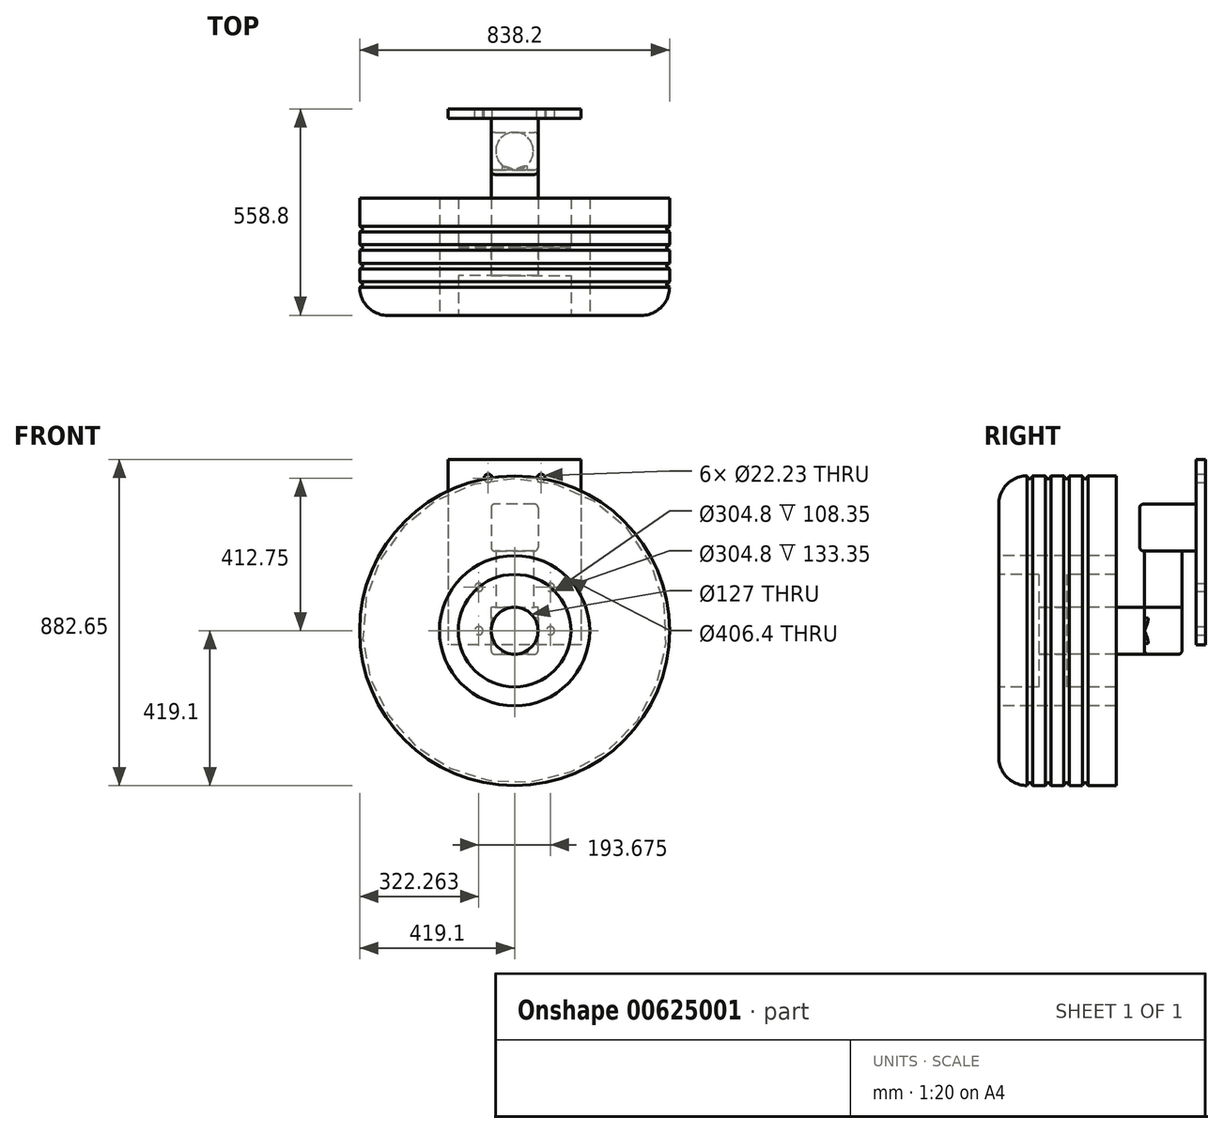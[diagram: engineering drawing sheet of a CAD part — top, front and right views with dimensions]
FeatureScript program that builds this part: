
annotation { "Feature Type Name" : "Feature", "Feature Type Description" : "" }
export const myFeature = defineFeature(function(context is Context, id is Id, definition is map)
    precondition{}
    {
        {
            var Q0;
            Q0=qCreatedBy(makeId("Right.planeOp"),FACE);
            var sketch = newSketch(context, id + "F0", { "sketchPlane" : qUnion([Q0])});
            skLineSegment(sketch, "E0", {"start": v(-439.18, 0) * mm, "end": v(305.36, 0) * mm, "construction": true});
            skLineSegment(sketch, "E1", {"start": v(-158.75, 203.2) * mm, "end": v(-158.75, 152.4) * mm});
            skLineSegment(sketch, "E2", {"start": v(-158.75, 203.2) * mm, "end": v(158.75, 203.2) * mm});
            skLineSegment(sketch, "E3", {"start": v(158.75, 203.2) * mm, "end": v(158.75, 152.4) * mm});
            skLineSegment(sketch, "E4", {"start": v(0, 509.7) * mm, "end": v(0, -178.07) * mm, "construction": true});
            skPoint(sketch, "E5", {"position": v(0, 203.2) * mm});
            skLineSegment(sketch, "E6", {"start": v(-25.4, 0) * mm, "end": v(25.4, 0) * mm});
            skLineSegment(sketch, "E7", {"start": v(158.75, 152.4) * mm, "end": v(25.4, 152.4) * mm});
            skLineSegment(sketch, "E8", {"start": v(25.4, 152.4) * mm, "end": v(25.4, 0) * mm});
            skLineSegment(sketch, "E9.MirrorCS", {"start": v(-25.4, 152.4) * mm, "end": v(-25.4, 0) * mm});
            skLineSegment(sketch, "E10.MirrorCS", {"start": v(-158.75, 152.4) * mm, "end": v(-25.4, 152.4) * mm});
            skSolve(sketch);
        }
        {
            var Q0;
            Q0 = qSketchRegion(id + "F0", true);
            var Q1;
            Q1=sQuery(id+"F0.wireOp",EDGE,"E0");
            revolve(context, id + "F1", {"surfaceOperationType" : NewSurfaceOperationType.NEW, "entities" : qUnion([Q0]), "axis" : qUnion([Q1]), "revolveType" : RevolveType.FULL});
        }
        {
            var Q0;
            Q0=makeQuery(id+"F1.opRevolve","SWEPT_FACE",FACE,{"disambiguationData":[OSD([sQuery(id+"F0.wireOp",EDGE,"E8")])]});
            var sketch = newSketch(context, id + "F2", { "sketchPlane" : qUnion([Q0])});
            skCircle(sketch, "E11", {"center": v(0, 0) * mm, "radius": 63.5 * mm});
            skSolve(sketch);
        }
        {
            var Q0;
            Q0 = qSketchRegion(id + "F2", true);
            extrude(context, id + "F3", {"entities" : qUnion([Q0]), "operationType" : NewBodyOperationType.REMOVE, "endBound" : BoundingType.THROUGH_ALL, "oppositeDirection" : true, "depth" : 25 * mm, "offsetDistance" : 25 * mm});
        }
        {
            var Q0;
            Q0=makeQuery(id+"F1.opRevolve","SWEPT_FACE",FACE,{"disambiguationData":[OSD([sQuery(id+"F0.wireOp",EDGE,"E9.MirrorCS")])]});
            extrude(context, id + "F4", {"entities" : qUnion([Q0]), "operationType" : NewBodyOperationType.ADD, "depth" : 25 * mm, "offsetDistance" : 25 * mm});
        }
        {
            var Q0;
            Q0=makeQuery(id+"F4.opExtrude","CAP_FACE",FACE,{"disambiguationData":[OSD([sQuery(id+"F0.wireOp",EDGE,"E9.MirrorCS")])],"isStart":false});
            var sketch = newSketch(context, id + "F5", { "sketchPlane" : qUnion([Q0])});
            skCircle(sketch, "E12", {"center": v(0, 0) * mm, "radius": 63.5 * mm});
            skSolve(sketch);
        }
        {
            var Q0;
            Q0 = qSketchRegion(id + "F5", true);
            extrude(context, id + "F6", {"entities" : qUnion([Q0]), "oppositeDirection" : true, "depth" : 285.75 * mm, "offsetDistance" : 25 * mm});
        }
        {
            var Q0;
            Q0=makeQuery(id+"F1.opRevolve","SWEPT_FACE",FACE,{"disambiguationData":[OSD([sQuery(id+"F0.wireOp",EDGE,"E1")])]});
            var sketch = newSketch(context, id + "F7", { "sketchPlane" : qUnion([Q0])});
            skCircle(sketch, "E13", {"center": v(0, 0) * mm, "radius": 203.2 * mm});
            skCircle(sketch, "E14", {"center": v(0, 0) * mm, "radius": 419.1 * mm});
            skSolve(sketch);
        }
        {
            var Q0;
            Q0 = qSketchRegion(id + "F7", true);
            var Q1;
            Q1=makeQuery(id+"F1.opRevolve","SWEPT_FACE",FACE,{"disambiguationData":[OSD([sQuery(id+"F0.wireOp",EDGE,"E3")])]});
            extrude(context, id + "F8", {"entities" : qUnion([Q0]), "endBound" : BoundingType.UP_TO_SURFACE, "oppositeDirection" : true, "depth" : 25 * mm, "endBoundEntityFace" : qUnion([Q1]), "offsetDistance" : 25 * mm});
        }
        {
            var Q0;
            Q0=makeQuery(id+"F8.opExtrude","CAP_EDGE",EDGE,{"disambiguationData":[OSD([sQuery(id+"F7.wireOp",EDGE,"E14")])],"isStart":true});
            var Q1;
            Q1=makeQuery(id+"F8.opExtrude","TWEAK_EDGE",EDGE,{"derivedFrom":[makeQuery(id+"F1.opRevolve","SWEPT_FACE",FACE,{"disambiguationData":[OSD([sQuery(id+"F0.wireOp",EDGE,"E3")])]}),makeQuery(id+"F7.imprint","IMPRINT",EDGE,{"derivedFrom":sQuery(id+"F7.wireOp",EDGE,"E14")})]});
            fillet(context, id + "F9", {"entities" : qUnion([Q0, Q1]), "radius" : 76.2 * mm, "tangentPropagation" : true, "allowEdgeOverflow" : false});
        }
        {
            var Q0;
            Q0=qCreatedBy(makeId("Right.planeOp"),FACE);
            var sketch = newSketch(context, id + "F10", { "sketchPlane" : qUnion([Q0])});
            skPoint(sketch, "E15.middle", {"position": v(0, 0) * mm});
            skLineSegment(sketch, "E16", {"start": v(-287.93, 419.1) * mm, "end": v(273.21, 419.1) * mm, "construction": true});
            skLineSegment(sketch, "E17", {"start": v(-540.82, 0) * mm, "end": v(556.4, 0) * mm, "construction": true});
            skLineSegment(sketch, "E18", {"start": v(268.1, 406.4) * mm, "end": v(-286.95, 406.4) * mm, "construction": true});
            skLineSegment(sketch, "E19", {"start": v(-82.71, 419.1) * mm, "end": v(-82.71, 406.4) * mm, "construction": true});
            skLineSegment(sketch, "E20", {"start": v(-82.71, 419.1) * mm, "end": v(-79.47, 413.64) * mm});
            skLineSegment(sketch, "E21", {"start": v(-70.87, 413.64) * mm, "end": v(-67.63, 419.1) * mm});
            skLineSegment(sketch, "E22", {"start": v(-67.63, 419.1) * mm, "end": v(-82.71, 419.1) * mm});
            skPoint(sketch, "E23.visualSharp", {"position": v(-75.17, 406.4) * mm});
            skArc(sketch, "E23.filletArc", {"start": v(-79.47, 413.64) * mm, "mid": v(-75.17, 411.2) * mm, "end": v(-70.87, 413.64) * mm});
            skLineSegment(sketch, "E24", {"start": v(0, 0) * mm, "end": v(0, 599.85) * mm, "construction": true});
            skLineSegment(sketch, "E25", {"start": v(-82.71, 419.1) * mm, "end": v(-67.63, 419.1) * mm});
            skArc(sketch, "E26.1.0.0", {"start": v(-29.47, 413.64) * mm, "mid": v(-25.17, 411.2) * mm, "end": v(-20.87, 413.64) * mm});
            skLineSegment(sketch, "E26.1.0.1", {"start": v(-32.71, 419.1) * mm, "end": v(-29.47, 413.64) * mm});
            skLineSegment(sketch, "E26.1.0.2", {"start": v(-20.87, 413.64) * mm, "end": v(-17.63, 419.1) * mm});
            skLineSegment(sketch, "E26.1.0.3", {"start": v(-32.71, 419.1) * mm, "end": v(-17.63, 419.1) * mm});
            skArc(sketch, "E26.2.0.0", {"start": v(20.53, 413.64) * mm, "mid": v(24.83, 411.2) * mm, "end": v(29.13, 413.64) * mm});
            skLineSegment(sketch, "E26.2.0.1", {"start": v(17.29, 419.1) * mm, "end": v(20.53, 413.64) * mm});
            skLineSegment(sketch, "E26.2.0.2", {"start": v(29.13, 413.64) * mm, "end": v(32.37, 419.1) * mm});
            skLineSegment(sketch, "E26.2.0.3", {"start": v(17.29, 419.1) * mm, "end": v(32.37, 419.1) * mm});
            skArc(sketch, "E26.3.0.0", {"start": v(70.53, 413.64) * mm, "mid": v(74.83, 411.2) * mm, "end": v(79.13, 413.64) * mm});
            skLineSegment(sketch, "E26.3.0.1", {"start": v(67.29, 419.1) * mm, "end": v(70.53, 413.64) * mm});
            skLineSegment(sketch, "E26.3.0.2", {"start": v(79.13, 413.64) * mm, "end": v(82.37, 419.1) * mm});
            skLineSegment(sketch, "E26.3.0.3", {"start": v(67.29, 419.1) * mm, "end": v(82.37, 419.1) * mm});
            skLineSegment(sketch, "E26.direction1", {"start": v(-79.47, 413.64) * mm, "end": v(-29.47, 413.64) * mm, "construction": true});
            skSolve(sketch);
        }
        {
            var Q0;
            Q0 = qSketchRegion(id + "F10", true);
            var Q1;
            Q1=sQuery(id+"F10.wireOp",EDGE,"E17");
            revolve(context, id + "F11", {"operationType" : NewBodyOperationType.REMOVE, "surfaceOperationType" : NewSurfaceOperationType.NEW, "entities" : qUnion([Q0]), "axis" : qUnion([Q1]), "revolveType" : RevolveType.FULL, "oppositeDirection" : true});
        }
        {
            var Q0;
            Q0=makeQuery(id+"F6.opExtrude","CAP_FACE",FACE,{"disambiguationData":[OSD([sQuery(id+"F5.wireOp",EDGE,"E12")])],"isStart":false});
            var sketch = newSketch(context, id + "F12", { "sketchPlane" : qUnion([Q0])});
            skLineSegment(sketch, "E27.bottom", {"start": v(63.5, -63.5) * mm, "end": v(-63.5, -63.5) * mm});
            skLineSegment(sketch, "E27.top", {"start": v(63.5, 63.5) * mm, "end": v(-63.5, 63.5) * mm});
            skLineSegment(sketch, "E27.left", {"start": v(63.5, -63.5) * mm, "end": v(63.5, 63.5) * mm});
            skLineSegment(sketch, "E27.right", {"start": v(-63.5, -63.5) * mm, "end": v(-63.5, 63.5) * mm});
            skPoint(sketch, "E27.middle", {"position": v(0, 0) * mm});
            skSolve(sketch);
        }
        {
            var Q0;
            Q0 = qSketchRegion(id + "F12", true);
            extrude(context, id + "F13", {"entities" : qUnion([Q0]), "operationType" : NewBodyOperationType.ADD, "depth" : 101.6 * mm, "offsetDistance" : 25 * mm});
        }
        {
            var Q0;
            Q0=makeQuery(id+"F13.opExtrude","SWEPT_FACE",FACE,{"disambiguationData":[OSD([sQuery(id+"F12.wireOp",EDGE,"E27.top")])]});
            var sketch = newSketch(context, id + "F14", { "sketchPlane" : qUnion([Q0])});
            skCircle(sketch, "E28", {"center": v(0, 286.15) * mm, "radius": 50.8 * mm});
            skSolve(sketch);
        }
        {
            var Q0;
            Q0 = qSketchRegion(id + "F14", true);
            extrude(context, id + "F15", {"entities" : qUnion([Q0]), "operationType" : NewBodyOperationType.ADD, "depth" : 152.4 * mm, "offsetDistance" : 25 * mm});
        }
        {
            var Q0;
            Q0=makeQuery(id+"F15.opExtrude","CAP_FACE",FACE,{"disambiguationData":[OSD([sQuery(id+"F14.wireOp",EDGE,"E28")])],"isStart":false});
            var sketch = newSketch(context, id + "F16", { "sketchPlane" : qUnion([Q0])});
            skLineSegment(sketch, "E29.bottom", {"start": v(63.5, 349.65) * mm, "end": v(-63.5, 349.65) * mm});
            skLineSegment(sketch, "E29.top", {"start": v(63.5, 222.65) * mm, "end": v(-63.5, 222.65) * mm});
            skLineSegment(sketch, "E29.left", {"start": v(63.5, 349.65) * mm, "end": v(63.5, 222.65) * mm});
            skLineSegment(sketch, "E29.right", {"start": v(-63.5, 349.65) * mm, "end": v(-63.5, 222.65) * mm});
            skPoint(sketch, "E29.middle", {"position": v(0, 286.15) * mm});
            skSolve(sketch);
        }
        {
            var Q0;
            Q0 = qSketchRegion(id + "F16", true);
            extrude(context, id + "F17", {"entities" : qUnion([Q0]), "operationType" : NewBodyOperationType.ADD, "depth" : 127 * mm, "offsetDistance" : 25 * mm});
        }
        {
            var Q0;
            Q0=makeQuery(id+"F17.opExtrude","SWEPT_FACE",FACE,{"disambiguationData":[OSD([sQuery(id+"F16.wireOp",EDGE,"E29.bottom")])]});
            extrude(context, id + "F18", {"entities" : qUnion([Q0]), "operationType" : NewBodyOperationType.ADD, "depth" : 25 * mm, "offsetDistance" : 25 * mm});
        }
        {
            var Q0;
            Q0=makeQuery(id+"F18.opExtrude","CAP_FACE",FACE,{"disambiguationData":[OSD([sQuery(id+"F16.wireOp",EDGE,"E29.bottom")])],"isStart":false});
            var sketch = newSketch(context, id + "F19", { "sketchPlane" : qUnion([Q0])});
            skLineSegment(sketch, "E30.bottom", {"start": v(-179.39, 463.55) * mm, "end": v(179.39, 463.55) * mm});
            skLineSegment(sketch, "E30.top", {"start": v(-179.39, -38.1) * mm, "end": v(179.39, -38.1) * mm});
            skLineSegment(sketch, "E30.left", {"start": v(-179.39, 463.55) * mm, "end": v(-179.39, -38.1) * mm});
            skLineSegment(sketch, "E30.right", {"start": v(179.39, 463.55) * mm, "end": v(179.39, -38.1) * mm});
            skLineSegment(sketch, "E31", {"start": v(0, 463.55) * mm, "end": v(0, -82.83) * mm, "construction": true});
            skLineSegment(sketch, "E32", {"start": v(-556.4, 0) * mm, "end": v(580.96, 0) * mm, "construction": true});
            skSolve(sketch);
        }
        {
            var Q0;
            Q0 = qSketchRegion(id + "F19", true);
            extrude(context, id + "F20", {"entities" : qUnion([Q0]), "operationType" : NewBodyOperationType.ADD, "depth" : 25.4 * mm, "offsetDistance" : 25 * mm});
        }
        {
            var Q0;
            {var subQ0=sQuery(id+"F16.wireOp",EDGE,"E29.left");var subQ1=sQuery(id+"F16.wireOp",EDGE,"E29.bottom");Q0=makeQuery(id+"F18.boolean.opBoolean","MERGE",EDGE,{"derivedFrom":[makeQuery(id+"F17.opExtrude","CAP_EDGE",EDGE,{"disambiguationData":[OSD([subQ0])],"isStart":false}),makeQuery(id+"F18.opExtrude","SWEPT_EDGE",EDGE,{"disambiguationData":[OSD([subQ1,subQ0]),TDD([makeQuery(id+"F17.opExtrude","CAP_VERTEX",VERTEX,{"disambiguationData":[OSD([subQ1,subQ0])],"isStart":false})])]})]});}
            var Q1;
            {var subQ0=sQuery(id+"F16.wireOp",EDGE,"E29.right");var subQ1=sQuery(id+"F16.wireOp",EDGE,"E29.bottom");Q1=makeQuery(id+"F18.boolean.opBoolean","MERGE",EDGE,{"derivedFrom":[makeQuery(id+"F17.opExtrude","CAP_EDGE",EDGE,{"disambiguationData":[OSD([subQ0])],"isStart":false}),makeQuery(id+"F18.opExtrude","SWEPT_EDGE",EDGE,{"disambiguationData":[OSD([subQ1,subQ0]),TDD([makeQuery(id+"F17.opExtrude","CAP_VERTEX",VERTEX,{"disambiguationData":[OSD([subQ1,subQ0])],"isStart":false})])]})]});}
            var Q2;
            Q2=makeQuery(id+"F17.opExtrude","SWEPT_EDGE",EDGE,{"disambiguationData":[OSD([sQuery(id+"F16.wireOp",EDGE,"E29.top"),sQuery(id+"F16.wireOp",EDGE,"E29.left")])]});
            var Q3;
            Q3=makeQuery(id+"F17.opExtrude","SWEPT_EDGE",EDGE,{"disambiguationData":[OSD([sQuery(id+"F16.wireOp",EDGE,"E29.top"),sQuery(id+"F16.wireOp",EDGE,"E29.right")])]});
            var Q4;
            Q4=makeQuery(id+"F13.opExtrude","SWEPT_EDGE",EDGE,{"disambiguationData":[OSD([sQuery(id+"F12.wireOp",EDGE,"E27.bottom"),sQuery(id+"F12.wireOp",EDGE,"E27.right")])]});
            var Q5;
            Q5=makeQuery(id+"F13.opExtrude","SWEPT_EDGE",EDGE,{"disambiguationData":[OSD([sQuery(id+"F12.wireOp",EDGE,"E27.bottom"),sQuery(id+"F12.wireOp",EDGE,"E27.left")])]});
            var Q6;
            Q6=makeQuery(id+"F13.opExtrude","CAP_EDGE",EDGE,{"disambiguationData":[OSD([sQuery(id+"F12.wireOp",EDGE,"E27.right")])],"isStart":false});
            var Q7;
            Q7=makeQuery(id+"F13.opExtrude","CAP_EDGE",EDGE,{"disambiguationData":[OSD([sQuery(id+"F12.wireOp",EDGE,"E27.left")])],"isStart":false});
            var Q8;
            {var subQ0=sQuery(id+"F12.wireOp",EDGE,"E27.bottom");var subQ1=sQuery(id+"F12.wireOp",EDGE,"E27.right");Q8=makeQuery(id+"F13.boolean.opBoolean","SPLIT",EDGE,{"disambiguationData":[TD([makeQuery(id+"F13.opExtrude","SWEPT_FACE",FACE,{"disambiguationData":[OSD([subQ0])]})])],"derivedFrom":makeQuery(id+"F13.opExtrude","CAP_EDGE",EDGE,{"disambiguationData":[OSD([subQ1])],"isStart":true})});}
            var Q9;
            {var subQ0=sQuery(id+"F12.wireOp",EDGE,"E27.right");var subQ1=sQuery(id+"F12.wireOp",EDGE,"E27.top");Q9=makeQuery(id+"F13.boolean.opBoolean","SPLIT",EDGE,{"disambiguationData":[TD([makeQuery(id+"F13.opExtrude","SWEPT_FACE",FACE,{"disambiguationData":[OSD([subQ1])]})])],"derivedFrom":makeQuery(id+"F13.opExtrude","CAP_EDGE",EDGE,{"disambiguationData":[OSD([subQ0])],"isStart":true})});}
            var Q10;
            {var subQ0=sQuery(id+"F12.wireOp",EDGE,"E27.left");var subQ1=sQuery(id+"F12.wireOp",EDGE,"E27.top");Q10=makeQuery(id+"F13.boolean.opBoolean","SPLIT",EDGE,{"disambiguationData":[TD([makeQuery(id+"F13.opExtrude","SWEPT_FACE",FACE,{"disambiguationData":[OSD([subQ1])]})])],"derivedFrom":makeQuery(id+"F13.opExtrude","CAP_EDGE",EDGE,{"disambiguationData":[OSD([subQ0])],"isStart":true})});}
            var Q11;
            {var subQ0=sQuery(id+"F12.wireOp",EDGE,"E27.left");var subQ1=sQuery(id+"F12.wireOp",EDGE,"E27.bottom");Q11=makeQuery(id+"F13.boolean.opBoolean","SPLIT",EDGE,{"disambiguationData":[TD([makeQuery(id+"F13.opExtrude","SWEPT_FACE",FACE,{"disambiguationData":[OSD([subQ1])]})])],"derivedFrom":makeQuery(id+"F13.opExtrude","CAP_EDGE",EDGE,{"disambiguationData":[OSD([subQ0])],"isStart":true})});}
            var Q12;
            {var subQ0=sQuery(id+"F16.wireOp",EDGE,"E29.right");var subQ1=sQuery(id+"F16.wireOp",EDGE,"E29.bottom");Q12=makeQuery(id+"F18.boolean.opBoolean","MERGE",EDGE,{"derivedFrom":[makeQuery(id+"F17.opExtrude","CAP_EDGE",EDGE,{"disambiguationData":[OSD([subQ0])],"isStart":true}),makeQuery(id+"F18.opExtrude","SWEPT_EDGE",EDGE,{"disambiguationData":[OSD([subQ1,subQ0]),TDD([makeQuery(id+"F17.opExtrude","CAP_VERTEX",VERTEX,{"disambiguationData":[OSD([subQ1,subQ0])],"isStart":true})])]})]});}
            var Q13;
            {var subQ0=sQuery(id+"F16.wireOp",EDGE,"E29.left");var subQ1=sQuery(id+"F16.wireOp",EDGE,"E29.bottom");Q13=makeQuery(id+"F18.boolean.opBoolean","MERGE",EDGE,{"derivedFrom":[makeQuery(id+"F17.opExtrude","CAP_EDGE",EDGE,{"disambiguationData":[OSD([subQ0])],"isStart":true}),makeQuery(id+"F18.opExtrude","SWEPT_EDGE",EDGE,{"disambiguationData":[OSD([subQ1,subQ0]),TDD([makeQuery(id+"F17.opExtrude","CAP_VERTEX",VERTEX,{"disambiguationData":[OSD([subQ1,subQ0])],"isStart":true})])]})]});}
            var Q14;
            Q14=makeQuery(id+"F17.opExtrude","CAP_EDGE",EDGE,{"disambiguationData":[OSD([sQuery(id+"F16.wireOp",EDGE,"E29.top")])],"isStart":true});
            var Q15;
            Q15=makeQuery(id+"F17.opExtrude","CAP_EDGE",EDGE,{"disambiguationData":[OSD([sQuery(id+"F16.wireOp",EDGE,"E29.top")])],"isStart":false});
            var Q16;
            Q16=makeQuery(id+"F13.opExtrude","CAP_EDGE",EDGE,{"disambiguationData":[OSD([sQuery(id+"F12.wireOp",EDGE,"E27.bottom")])],"isStart":false});
            var Q17;
            {var subQ0=sQuery(id+"F12.wireOp",EDGE,"E27.bottom");var subQ1=sQuery(id+"F12.wireOp",EDGE,"E27.right");Q17=makeQuery(id+"F13.boolean.opBoolean","SPLIT",EDGE,{"disambiguationData":[TD([makeQuery(id+"F13.opExtrude","SWEPT_FACE",FACE,{"disambiguationData":[OSD([subQ1])]})])],"derivedFrom":makeQuery(id+"F13.opExtrude","CAP_EDGE",EDGE,{"disambiguationData":[OSD([subQ0])],"isStart":true})});}
            var Q18;
            {var subQ0=sQuery(id+"F12.wireOp",EDGE,"E27.left");var subQ1=sQuery(id+"F12.wireOp",EDGE,"E27.bottom");Q18=makeQuery(id+"F13.boolean.opBoolean","SPLIT",EDGE,{"disambiguationData":[TD([makeQuery(id+"F13.opExtrude","SWEPT_FACE",FACE,{"disambiguationData":[OSD([subQ0])]})])],"derivedFrom":makeQuery(id+"F13.opExtrude","CAP_EDGE",EDGE,{"disambiguationData":[OSD([subQ1])],"isStart":true})});}
            fillet(context, id + "F21", {"entities" : qUnion([Q0, Q1, Q2, Q3, Q4, Q5, Q6, Q7, Q8, Q9, Q10, Q11, Q12, Q13, Q14, Q15, Q16, Q17, Q18]), "radius" : 10 * mm, "tangentPropagation" : true, "allowEdgeOverflow" : false});
        }
        {
            var Q0;
            Q0=makeQuery(id+"F20.opExtrude","CAP_FACE",FACE,{"disambiguationData":[OSD([sQuery(id+"F19.wireOp",EDGE,"E30.bottom"),sQuery(id+"F19.wireOp",EDGE,"E30.top"),sQuery(id+"F19.wireOp",EDGE,"E30.left"),sQuery(id+"F19.wireOp",EDGE,"E30.right")])],"isStart":false});
            var sketch = newSketch(context, id + "F22", { "sketchPlane" : qUnion([Q0])});
            skCircle(sketch, "E33", {"center": v(-96.84, 0) * mm, "radius": 11.11 * mm});
            skLineSegment(sketch, "E34", {"start": v(0, 463.55) * mm, "end": v(0, -38.1) * mm, "construction": true});
            skLineSegment(sketch, "E35", {"start": v(-96.84, 0) * mm, "end": v(-96.84, 159.56) * mm, "construction": true});
            skCircle(sketch, "E36", {"center": v(-96.84, 117.48) * mm, "radius": 11.11 * mm});
            skCircle(sketch, "E37", {"center": v(-71.44, 412.75) * mm, "radius": 11.11 * mm});
            skCircle(sketch, "E38.MirrorC", {"center": v(71.44, 412.75) * mm, "radius": 11.11 * mm});
            skCircle(sketch, "E39.MirrorC", {"center": v(96.84, 117.48) * mm, "radius": 11.11 * mm});
            skCircle(sketch, "E40.MirrorC", {"center": v(96.84, 0) * mm, "radius": 11.11 * mm});
            skSolve(sketch);
        }
        {
            var Q0;
            Q0 = qSketchRegion(id + "F22", true);
            extrude(context, id + "F23", {"entities" : qUnion([Q0]), "operationType" : NewBodyOperationType.REMOVE, "oppositeDirection" : true, "depth" : 25.4 * mm, "offsetDistance" : 25 * mm});
        }
    });
